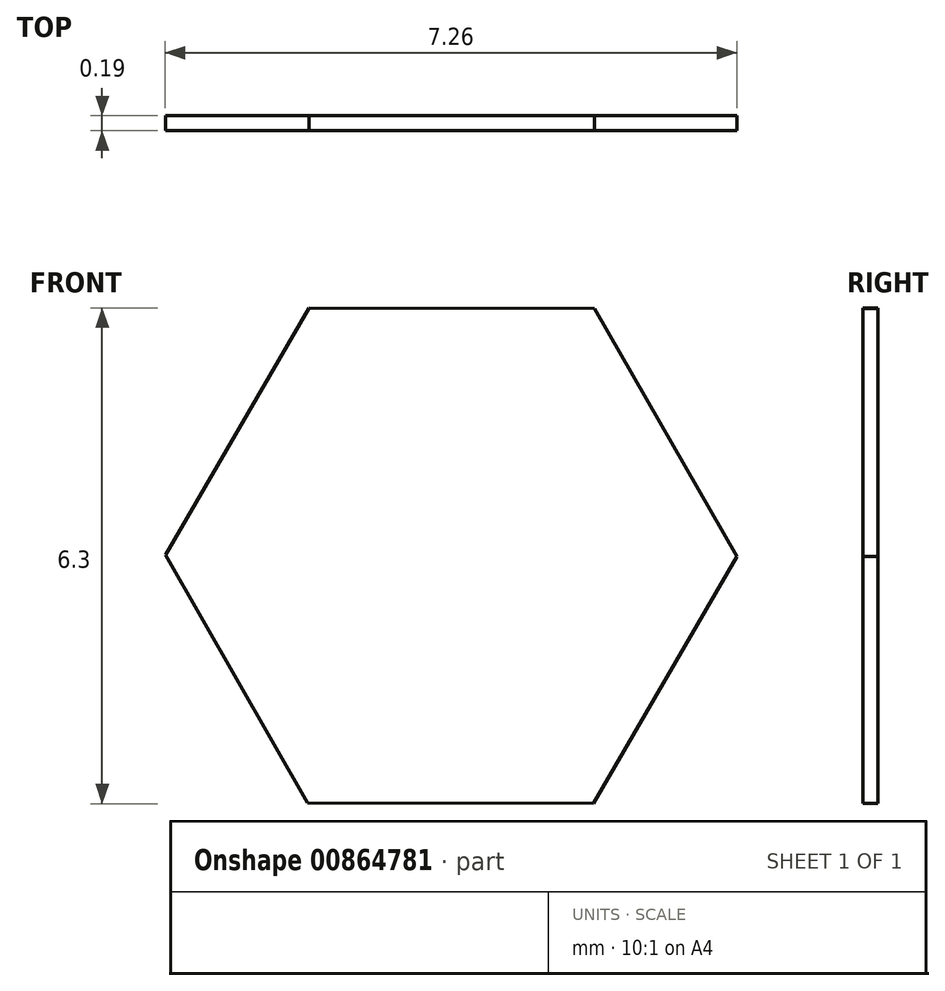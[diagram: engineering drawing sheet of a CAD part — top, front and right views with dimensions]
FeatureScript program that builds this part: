
annotation { "Feature Type Name" : "Feature", "Feature Type Description" : "" }
export const myFeature = defineFeature(function(context is Context, id is Id, definition is map)
    precondition{}
    {
        {
            assignVariable(context, id + "F0", {"name" : "H", "anyValue" : .188});
        }
        {
            var Q0;
            Q0=qCreatedBy(makeId("Front.planeOp"),FACE);
            var sketch = newSketch(context, id + "F1", { "sketchPlane" : qUnion([Q0])});
            skCircle(sketch, "E0.cCircle", {"center": v(0, 0) * mm, "radius": 3.14 * mm, "construction": true});
            skLineSegment(sketch, "E0.0", {"start": v(1.82, 3.14) * mm, "end": v(3.63, 0) * mm});
            skLineSegment(sketch, "E0.1", {"start": v(3.63, 0) * mm, "end": v(1.8, -3.15) * mm});
            skLineSegment(sketch, "E0.2", {"start": v(1.8, -3.15) * mm, "end": v(-1.82, -3.14) * mm});
            skLineSegment(sketch, "E0.3", {"start": v(-1.82, -3.14) * mm, "end": v(-3.63, 0) * mm});
            skLineSegment(sketch, "E0.4", {"start": v(-3.63, 0) * mm, "end": v(-1.8, 3.15) * mm});
            skLineSegment(sketch, "E0.5", {"start": v(-1.8, 3.15) * mm, "end": v(1.82, 3.14) * mm});
            skPoint(sketch, "E0.0.midPoint", {"position": v(2.73, 1.56) * mm});
            skSolve(sketch);
        }
        {
            var Q0;
            Q0 = qSketchRegion(id + "F1", true);
            extrude(context, id + "F2", {"entities" : qUnion([Q0]), "depth" : (getVariable(context, 'H')) * mm, "offsetDistance" : 25.4 * mm});
        }
    });
